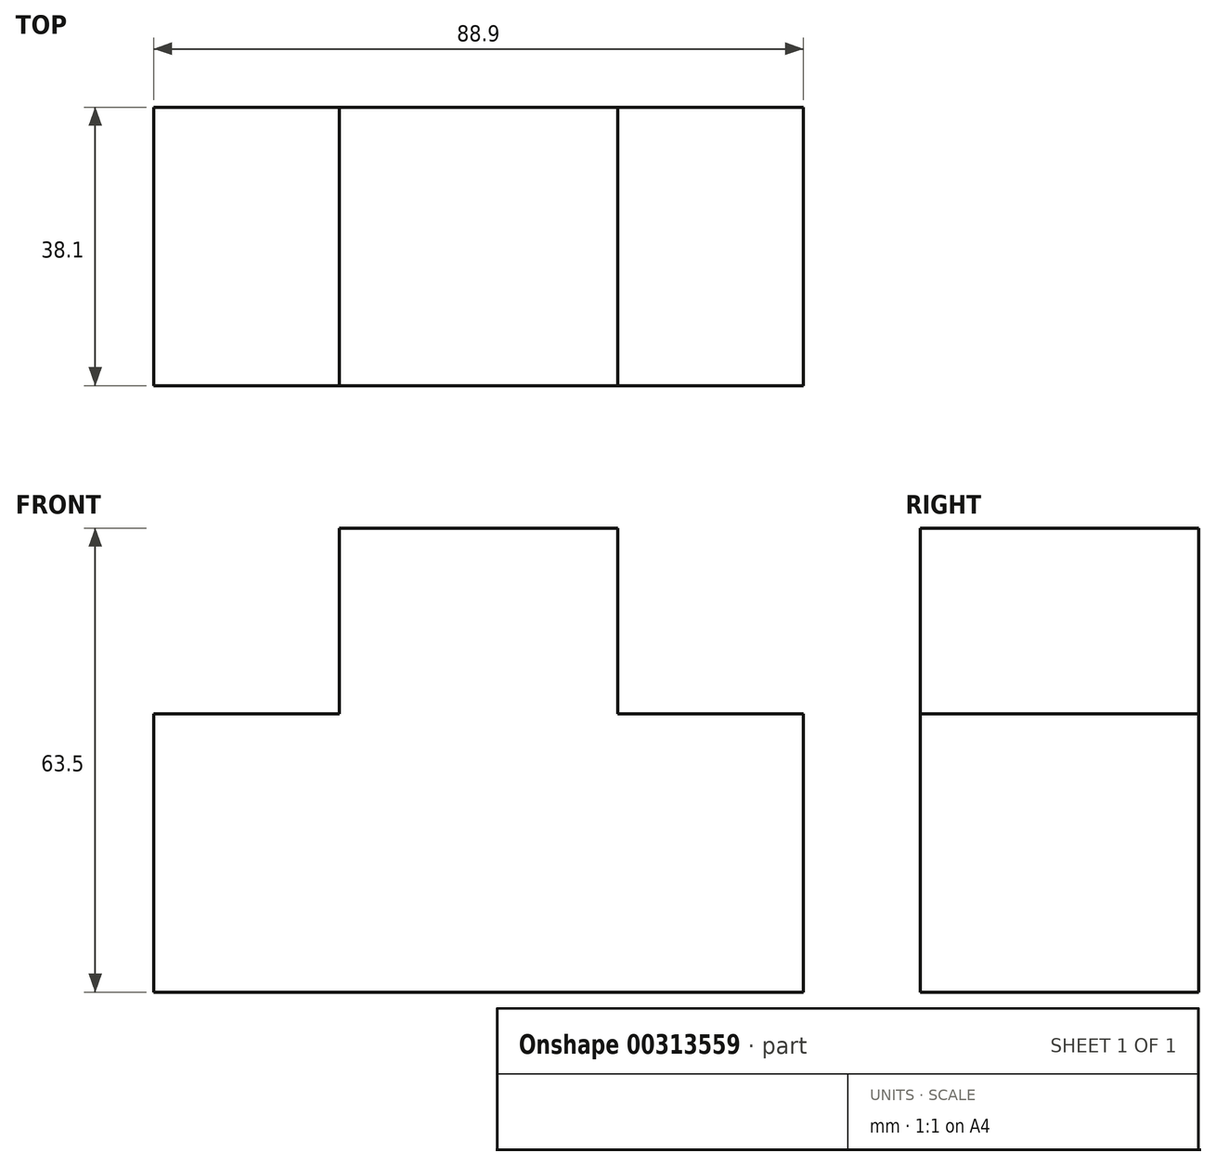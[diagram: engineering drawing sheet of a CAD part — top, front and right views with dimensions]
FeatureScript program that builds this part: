
annotation { "Feature Type Name" : "Feature", "Feature Type Description" : "" }
export const myFeature = defineFeature(function(context is Context, id is Id, definition is map)
    precondition{}
    {
        {
            var Q0;
            Q0=qCreatedBy(makeId("Front.planeOp"),FACE);
            var sketch = newSketch(context, id + "F0", { "sketchPlane" : qUnion([Q0])});
            skLineSegment(sketch, "E0", {"start": v(-31.45, -41.15) * mm, "end": v(57.45, -41.15) * mm});
            skLineSegment(sketch, "E1", {"start": v(57.45, -41.15) * mm, "end": v(57.45, -3.05) * mm});
            skLineSegment(sketch, "E2", {"start": v(57.45, -3.05) * mm, "end": v(32.05, -3.05) * mm});
            skLineSegment(sketch, "E3", {"start": v(32.05, -3.05) * mm, "end": v(32.05, 22.35) * mm});
            skLineSegment(sketch, "E4", {"start": v(32.05, 22.35) * mm, "end": v(-6.05, 22.35) * mm});
            skLineSegment(sketch, "E5", {"start": v(-6.05, 22.35) * mm, "end": v(-6.05, -3.05) * mm});
            skLineSegment(sketch, "E6", {"start": v(-6.05, -3.05) * mm, "end": v(-31.45, -3.05) * mm});
            skLineSegment(sketch, "E7", {"start": v(-31.45, -3.05) * mm, "end": v(-31.45, -41.15) * mm});
            skSolve(sketch);
        }
        {
            var Q0;
            Q0 = qSketchRegion(id + "F0", true);
            extrude(context, id + "F1", {"entities" : qUnion([Q0]), "oppositeDirection" : true, "depth" : 38.1 * mm});
        }
    });
